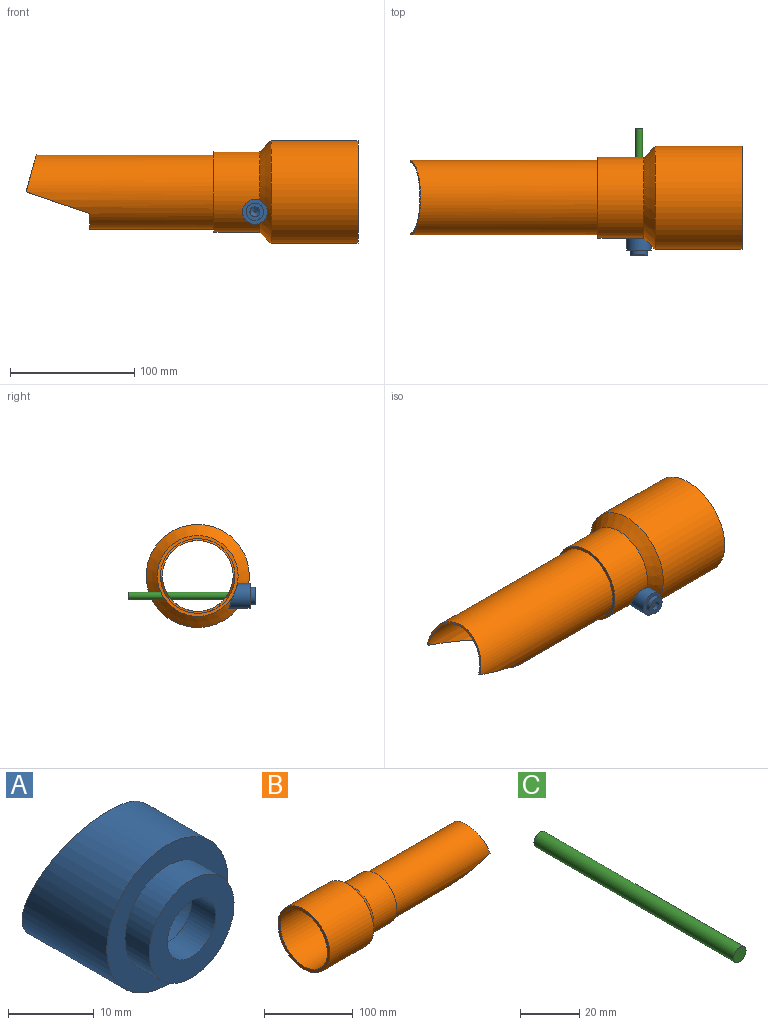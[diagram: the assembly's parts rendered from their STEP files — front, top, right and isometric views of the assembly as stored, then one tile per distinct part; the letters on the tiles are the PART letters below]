
ASSEMBLY  parts=3 mates=2
PART A: 10 faces, bbox 20x21x20 mm
  f0: cylinder r=10mm len=20mm, axis (0,-1,0), area 703mm2, adj f2,f4,f9
  f1: cylinder r=2.5mm len=11.27mm, axis (0,1,0), area 162.7mm2, adj f2,f8,f9
  f2: plane 19.95x15.64mm, normal (0,0.94,0.34), area 198.5mm2, adj f0,f1,f9
  f3: cone r=0mm half-angle=59deg, axis (0,-1,0), area 56.6mm2, adj f7,f8
  f4: plane 20x20mm, normal (0,-1,0), area 160.2mm2, adj f0,f5
  f5: cylinder r=7mm len=14mm, axis (0,-1,0), area 175.9mm2, adj f4,f6
  f6: plane 14x14mm, normal (0,-1,0), area 103.7mm2, adj f5,f7
  f7: cylinder r=4mm len=8mm, axis (0,-1,0), area 100.5mm2, adj f3,f6
  f8: cone r=0mm half-angle=59deg, axis (0,1,0), area 20.8mm2, adj f1,f3
  f9: plane 18.29x11.02mm, normal (0.71,0.71,0), area 152.7mm2, adj f0,f1,f2
PART B: 15 faces, bbox 267.3x83x83 mm
  f0: cylinder r=30mm len=151.31mm, axis (1,0,0), area 24096.5mm2, adj f2,f11,f12,f13,f14
  f1: cylinder r=28.5mm len=188.56mm, axis (1,0,0), area 29586.5mm2, adj f8,f9,f10,f11,f12,f13,f14
  f2: plane 65x65mm, normal (1,0,0), area 490.9mm2, adj f0,f3
  f3: cylinder r=32.5mm len=65mm, axis (1,0,0), area 7510mm2, adj f2,f4,f9,f10
  f4: cone r=41.5mm half-angle=45deg, axis (-1,0,0), area 2959mm2, adj f3,f5
  f5: cylinder r=41.5mm len=83mm, axis (1,0,0), area 18252.7mm2, adj f4,f6
  f6: plane 83x83mm, normal (-1,0,0), area 992.7mm2, adj f5,f7
  f7: cylinder r=37.5mm len=75mm, axis (1,0,0), area 16436.2mm2, adj f6,f8
  f8: cone r=37.5mm half-angle=45deg, axis (-1,0,0), area 2639.1mm2, adj f1,f7
  f9: cylinder r=2.5mm len=7.88mm, axis (0,-1,0), area 74.3mm2, adj f1,f3
  f10: cylinder r=2.5mm len=7.88mm, axis (0,-1,0), area 74.3mm2, adj f1,f3
  f11: plane 60x30mm, normal (0.96,0,0.27), area 143.2mm2, adj f0,f1,f12,f13
  f12: plane 51.37x17.41mm, normal (0.32,0,-0.95), area 87.2mm2, adj f0,f1,f11,f14
  f13: plane 51.37x17.41mm, normal (0.32,0,-0.95), area 87.2mm2, adj f0,f1,f11,f14
  f14: plane 48.86x12.59mm, normal (1,0,0), area 81.9mm2, adj f0,f1,f12,f13
PART C: 3 faces, bbox 6x95x6 mm
  f0: cylinder r=3mm len=95mm, axis (0,1,0), area 1790.7mm2, adj f1,f2
  f1: plane 6x6mm, normal (0,-1,0), area 28.3mm2, adj f0
  f2: plane 6x6mm, normal (0,1,0), area 28.3mm2, adj f0
PLACE A at identity fixed
PLACE B rot(axis=(0,0,1),180deg) t=(83,25.12,16)mm
PLACE C t=(0,80.48,0)mm
MATE cylindrical B.f9 <-> C.f0  axis (0,1,0) through (0,-4.49,0)mm
MATE revolute A.f1 <-> C.f0  axis (0,1,0) through (0,-14.52,0)mm
